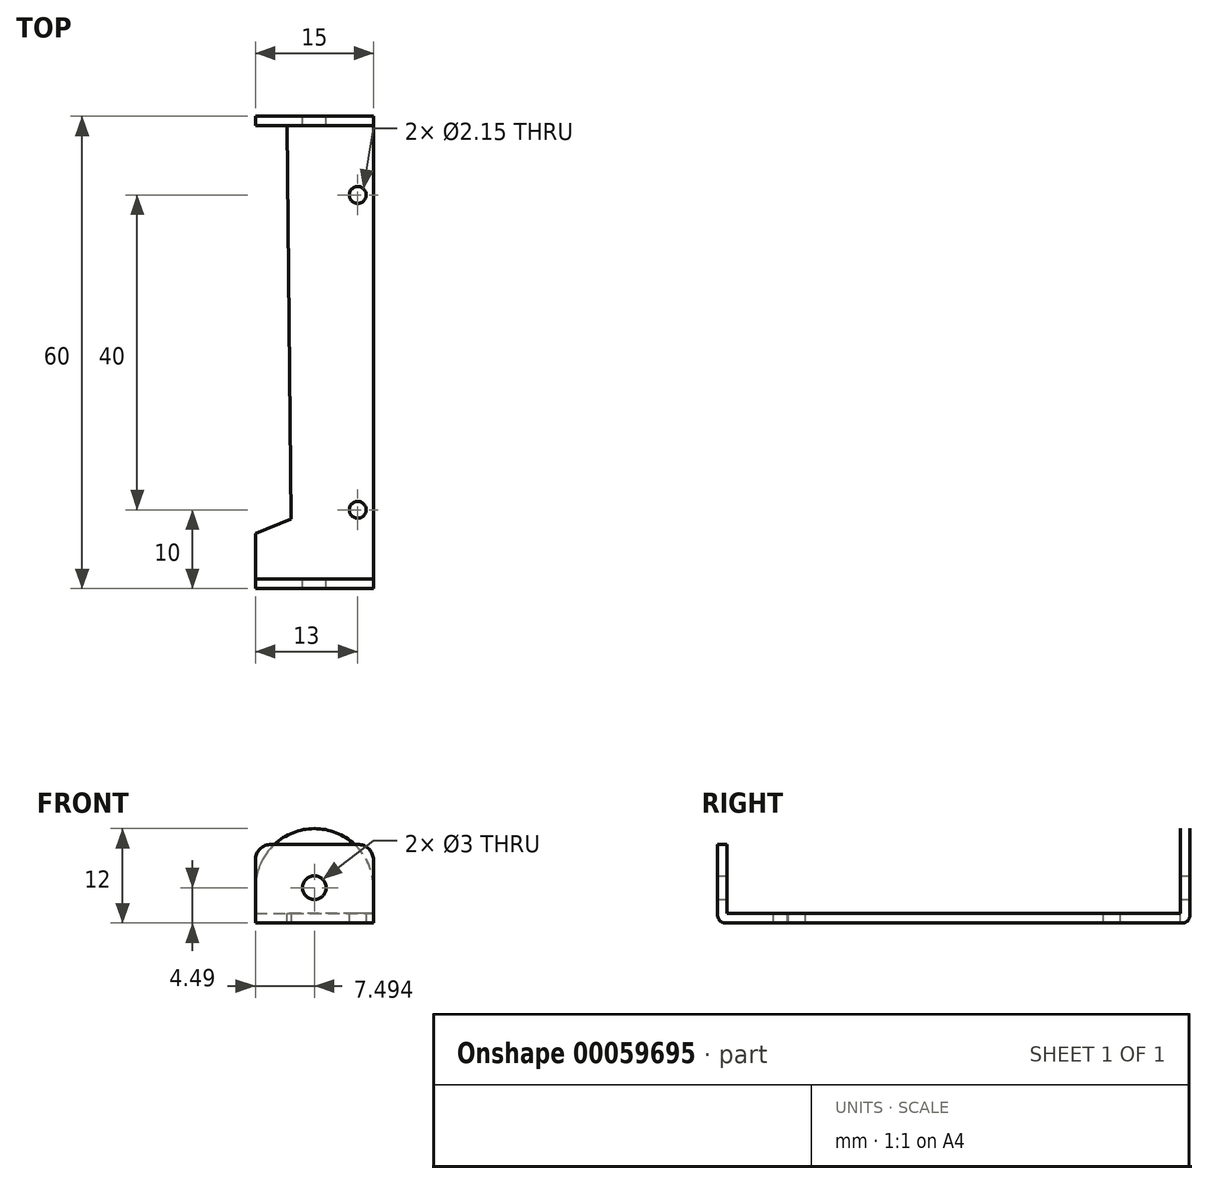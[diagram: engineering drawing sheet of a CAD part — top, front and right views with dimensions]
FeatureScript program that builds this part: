
annotation { "Feature Type Name" : "Feature", "Feature Type Description" : "" }
export const myFeature = defineFeature(function(context is Context, id is Id, definition is map)
    precondition{}
    {
        {
            var Q0;
            Q0=qCreatedBy(makeId("Top.planeOp"),FACE);
            var sketch = newSketch(context, id + "F0", { "sketchPlane" : qUnion([Q0])});
            skLineSegment(sketch, "E0", {"start": v(0, 0) * mm, "end": v(0, 60) * mm});
            skLineSegment(sketch, "E1", {"start": v(0, 60) * mm, "end": v(-15, 60) * mm});
            skLineSegment(sketch, "E2", {"start": v(-15, 7) * mm, "end": v(-15, 0) * mm});
            skLineSegment(sketch, "E3", {"start": v(-15, 0) * mm, "end": v(0, 0) * mm});
            skLineSegment(sketch, "E4", {"start": v(-15, 60) * mm, "end": v(-15, 58.8) * mm});
            skLineSegment(sketch, "E5", {"start": v(-15, 58.8) * mm, "end": v(-11, 58.8) * mm});
            skLineSegment(sketch, "E6", {"start": v(-11, 58.8) * mm, "end": v(-10.47, 8.8) * mm});
            skLineSegment(sketch, "E7", {"start": v(-15, 7) * mm, "end": v(-10.47, 8.8) * mm});
            skCircle(sketch, "E8", {"center": v(-2, 50) * mm, "radius": 1.07 * mm});
            skCircle(sketch, "E9", {"center": v(-2, 10) * mm, "radius": 1.07 * mm});
            skSolve(sketch);
        }
        {
            var Q0;
            Q0=makeQuery(id+"F0.imprint","IMPRINT",FACE,{"disambiguationData":[TD([[makeQuery(id+"F0.imprint","IMPRINT",EDGE,{"derivedFrom":sQuery(id+"F0.wireOp",EDGE,"E0")}),1.0]])]});
            var sketch = newSketch(context, id + "F1", { "sketchPlane" : qUnion([Q0])});
            skLineSegment(sketch, "E10", {"start": v(-15, 59.99) * mm, "end": v(-15, 58.79) * mm});
            skLineSegment(sketch, "E11", {"start": v(-15, 58.79) * mm, "end": v(0, 58.79) * mm});
            skLineSegment(sketch, "E12", {"start": v(0, 58.79) * mm, "end": v(0, 59.99) * mm});
            skLineSegment(sketch, "E13", {"start": v(0, 59.99) * mm, "end": v(-15, 59.99) * mm});
            skSolve(sketch);
        }
        {
            var Q0;
            Q0=makeQuery(id+"F0.imprint","IMPRINT",FACE,{"disambiguationData":[TD([[makeQuery(id+"F0.imprint","IMPRINT",EDGE,{"derivedFrom":sQuery(id+"F0.wireOp",EDGE,"E0")}),1.0]])]});
            var sketch = newSketch(context, id + "F2", { "sketchPlane" : qUnion([Q0])});
            skLineSegment(sketch, "E14", {"start": v(0, 0) * mm, "end": v(-15, 0) * mm});
            skLineSegment(sketch, "E15", {"start": v(-15, 0) * mm, "end": v(-15, 1.2) * mm});
            skLineSegment(sketch, "E16", {"start": v(-15, 1.2) * mm, "end": v(0, 1.2) * mm});
            skLineSegment(sketch, "E17", {"start": v(0, 1.2) * mm, "end": v(0, 0) * mm});
            skSolve(sketch);
        }
        {
            var Q0;
            Q0 = qSketchRegion(id + "F0", true);
            extrude(context, id + "F3", {"entities" : qUnion([Q0]), "depth" : 1.2 * mm});
        }
        {
            var Q0;
            Q0 = qSketchRegion(id + "F2", true);
            extrude(context, id + "F4", {"entities" : qUnion([Q0]), "operationType" : NewBodyOperationType.ADD, "depth" : 10 * mm});
        }
        {
            var Q0;
            Q0 = qSketchRegion(id + "F1", true);
            extrude(context, id + "F5", {"entities" : qUnion([Q0]), "operationType" : NewBodyOperationType.ADD, "depth" : 12 * mm});
        }
        {
            var Q0;
            Q0=makeQuery(id+"F5.opExtrude","CAP_EDGE",EDGE,{"disambiguationData":[OSD([sQuery(id+"F1.wireOp",EDGE,"E12")])],"isStart":false});
            var Q1;
            Q1=makeQuery(id+"F5.opExtrude","CAP_EDGE",EDGE,{"disambiguationData":[OSD([sQuery(id+"F1.wireOp",EDGE,"E10")])],"isStart":false});
            fillet(context, id + "F6", {"entities" : qUnion([Q0, Q1]), "radius" : 7.5 * mm, "tangentPropagation" : true, "allowEdgeOverflow" : false});
        }
        {
            var Q0;
            Q0=makeQuery(id+"F4.opExtrude","CAP_EDGE",EDGE,{"disambiguationData":[OSD([sQuery(id+"F2.wireOp",EDGE,"E17")])],"isStart":false});
            var Q1;
            Q1=makeQuery(id+"F4.opExtrude","CAP_EDGE",EDGE,{"disambiguationData":[OSD([sQuery(id+"F2.wireOp",EDGE,"E15")])],"isStart":false});
            fillet(context, id + "F7", {"entities" : qUnion([Q0, Q1]), "radius" : 2 * mm, "tangentPropagation" : true, "allowEdgeOverflow" : false});
        }
        {
            var Q0;
            Q0=makeQuery(id+"F3.opExtrude","CAP_EDGE",EDGE,{"disambiguationData":[OSD([sQuery(id+"F0.wireOp",EDGE,"E3")])],"isStart":true});
            var Q1;
            Q1=makeQuery(id+"F3.opExtrude","CAP_EDGE",EDGE,{"disambiguationData":[OSD([sQuery(id+"F0.wireOp",EDGE,"E1")])],"isStart":true});
            fillet(context, id + "F8", {"entities" : qUnion([Q0, Q1]), "radius" : 1 * mm, "tangentPropagation" : true, "allowEdgeOverflow" : false});
        }
        {
            var Q0;
            Q0=qCreatedBy(makeId("Front.planeOp"),FACE);
            var sketch = newSketch(context, id + "F9", { "sketchPlane" : qUnion([Q0])});
            skCircle(sketch, "E18", {"center": v(-7.5, 4.5) * mm, "radius": 7.5 * mm});
            skCircle(sketch, "E19", {"center": v(-7.5, 4.5) * mm, "radius": 1.5 * mm});
            skSolve(sketch);
        }
        {
            var Q0;
            Q0=sQuery(id+"F9.wireOp",VERTEX,"E18.center");
            var Q1;
            Q1=makeQuery(id+"F3.opExtrude","SWEPT_BODY",BODY,{"disambiguationData":[OSD([sQuery(id+"F0.wireOp",EDGE,"E0"),sQuery(id+"F0.wireOp",EDGE,"E1"),sQuery(id+"F0.wireOp",EDGE,"E2"),sQuery(id+"F0.wireOp",EDGE,"E3"),sQuery(id+"F0.wireOp",EDGE,"E4"),sQuery(id+"F0.wireOp",EDGE,"E5"),sQuery(id+"F0.wireOp",EDGE,"E6"),sQuery(id+"F0.wireOp",EDGE,"E7"),sQuery(id+"F0.wireOp",EDGE,"E8"),sQuery(id+"F0.wireOp",EDGE,"E9")])]});
            hole(context, id + "F10", {"style" : HoleStyle.SIMPLE, "holeDiameter" : 3 * mm, "endStyle" : HoleEndStyle.THROUGH, "locations" : qUnion([Q0]), "scope" : qUnion([Q1])});
        }
    });
